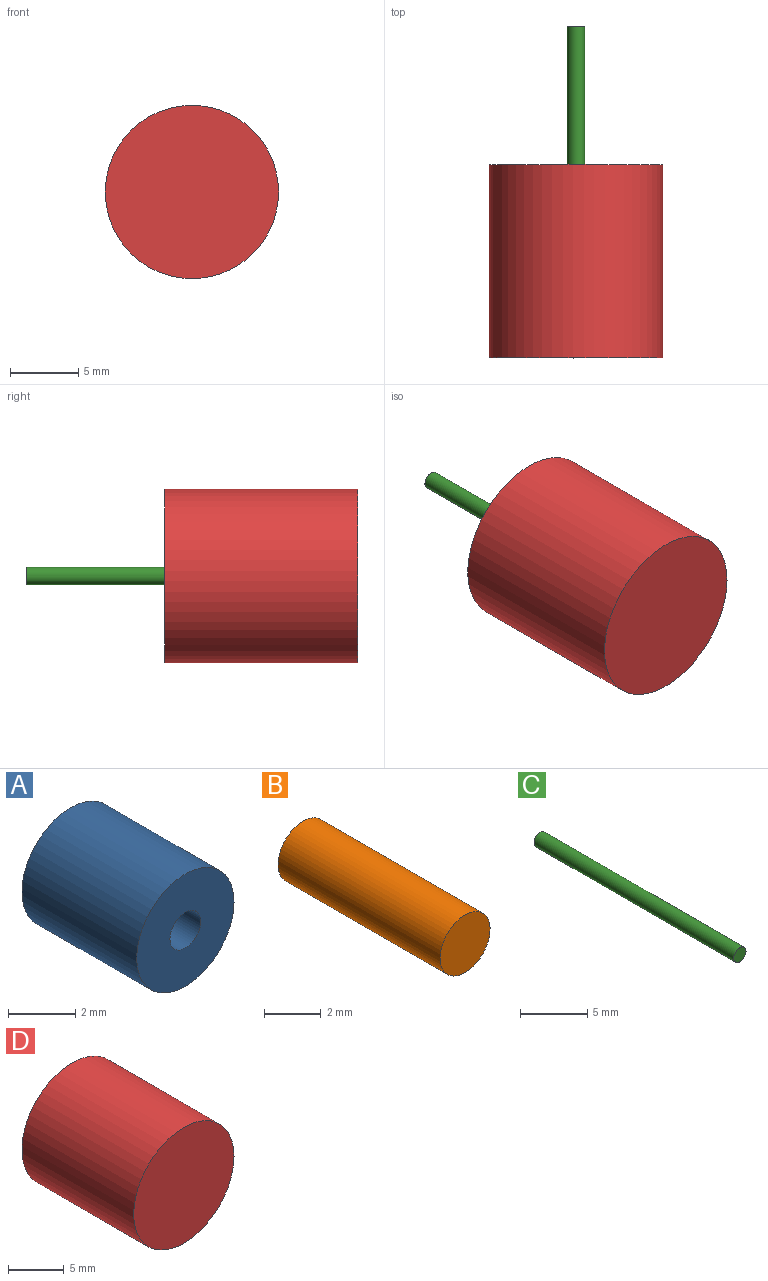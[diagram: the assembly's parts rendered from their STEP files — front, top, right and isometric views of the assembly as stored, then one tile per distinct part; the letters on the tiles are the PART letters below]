
ASSEMBLY  parts=4 mates=3
PART A: 4 faces, bbox 4.1x4.8x4.1 mm
  f0: cylinder r=2.04mm len=4.83mm, axis (0,1,0), area 62mm2, adj f1,f2
  f1: plane 4.09x4.09mm, normal (0,-1,0), area 11.8mm2, adj f0,f3
  f2: plane 4.09x4.09mm, normal (0,1,0), area 11.8mm2, adj f0,f3
  f3: cylinder r=0.65mm len=4.83mm, axis (0,-1,0), area 19.6mm2, adj f1,f2
PART B: 3 faces, bbox 2.5x8.1x2.5 mm
  f0: cylinder r=1.24mm len=8.08mm, axis (0,1,0), area 63.2mm2, adj f1,f2
  f1: plane 2.49x2.49mm, normal (0,-1,0), area 4.9mm2, adj f0
  f2: plane 2.49x2.49mm, normal (0,1,0), area 4.9mm2, adj f0
PART C: 3 faces, bbox 1.3x21x1.3 mm
  f0: cylinder r=0.64mm len=20.96mm, axis (0,1,0), area 83.6mm2, adj f1,f2
  f1: plane 1.27x1.27mm, normal (0,-1,0), area 1.3mm2, adj f0
  f2: plane 1.27x1.27mm, normal (0,1,0), area 1.3mm2, adj f0
PART D: 5 faces, bbox 12.7x14.2x12.7 mm
  f0: cylinder r=2.11mm len=4.83mm, axis (0,1,0), area 63.9mm2, adj f2,f3
  f1: cylinder r=6.35mm len=14.16mm, axis (0,1,0), area 565mm2, adj f2,f4
  f2: plane 12.7x12.7mm, normal (0,1,0), area 112.7mm2, adj f0,f1
  f3: plane 4.22x4.22mm, normal (0,1,0), area 14mm2, adj f0
  f4: plane 12.7x12.7mm, normal (0,-1,0), area 126.7mm2, adj f1
PLACE A t=(7.34,24.66,11.88)mm
PLACE B t=(7.34,29.49,11.88)mm
PLACE C t=(7.34,34.82,11.88)mm
PLACE D t=(7.34,24.66,11.88)mm
MATE cylindrical C.f0 <-> D.f0  axis (0,1,0) through (7.34,34.82,11.88)mm
MATE fastened D.f0 <-> A.f0  axis (0,1,0) through (7.34,24.66,11.88)mm
MATE cylindrical B.f0 <-> D.f0  axis (0,1,0) through (7.34,24.66,11.88)mm
